# Revit family: VLN_Nim-II-Mes-E_Multiproduct_BIM_NL_F3054;F3055
name_source: partatom
category: Plumbing Fixtures
revit_build: Autodesk Revit MEP 2014 (Build: 20130308_1515(x64)
units: mm (PartAtom-declared; Revit-internal decimal feet)

## types (2) — shared parameters
Accessories = www.idealstandardnederland.nl
AreaUnits = millimeters
Assembly Code = C1030200
AssetType = Vast
BREEAMApproved = No
Brand = Venlo
CodePerformance = EN 817, DIN 4109
Color = Chroom
ConnectionType = Sanitair
Default Elevation = 800 mm  [stored 2.62467 ft]
DurationUnit = jaar
ECA = No
ExpectedLife = 25
FaucetFunction = Mengkraan
FaucetOperation = Tweegreeps
FaucetType = Keukenmengkraan
Finish = Chroom
IfcExportAs = IfcValveType
IfcExportType = FAUCET
InstallationInstructions = http://www.idealstandardnederland.nl
LinearUnits = millimeters
ManufacturerURL = www.idealstandardnederland.nl
Material = Messing
NBSDescription = Water supply fittings for sinks
NBSReference = 45-35-70/345
NettWeight = 1.263 kg
NominalHeight = 297 mm
NominalLength = 217 mm
NominalWidth = 143 mm
ProductInformation = http://www.idealstandardnederland.nl
Shape = Gesculptuurd
Size = 143 x 217 x 297 mm
Space = Internal
SpareParts = www.idealstandardnederland.nl
TMV3 = Yes
TestPressure = 10 Bar
URL = www.idealstandardnederland.nl
Uniclass2015Code = Pr_40_20_87_84
Uniclass2015Title = Sink taps
Uniclass2015Version = Products v1.1
ValveMechanism = Keramische schijven
ValveOperation = Tweegreeps
Version = 1
VolumeUnits = liter
WRAS = No
WarrantyDescription = Fabrieksgarantie
WarrantyDurationParts = 10
WarrantyDurationUnit = jaar
WaterEfficientProduct = No
WorkingPressure = 1-5 bar
zero-valued in all types: CWFU, Cost, HWFU, WFU

## per-type parameters (varying)
| type | BIMObjectName | BarCode | Description | Features | FlowRate | Model | ModelNumber | ModelReference | Name |
| F3054AA - NIM-II-MES-E OPM T.FIX KEUKEN M KR 5L/MI | VLN_Venlo_SinkTaps_F3054AA | 8711678064721 | Venlo Nimbus II Messing keukenmengkraan 5 l/min eco. Eengats. Hoge draaibare uitloop. Straalregelaar. Sprong 200 mm. Hoogte uitloop 185 mm. Bovenbevestiging (TOP FIX). Eco bovendelen. Verloopset separaat bestellen. | Keukenmengkraan 5 l/min eco. Eengats. Hoge draaibare uitloop. Straalregelaar. Sprong 200 mm. Hoogte uitloop 185 mm. Bovenbevestiging (TOP FIX). Eco bovendelen. Verloopset separaat bestellen. | 5 liter @ 3 bar | F3054AA | F3054AA | Venlo Nimbus II Messing keukenmengkraan 5 l/min eco. Eengats. Hoge draaibare uitloop. Straalregelaar. Sprong 200 mm. Hoogte uitloop 185 mm. Bovenbevestiging (TOP FIX). Eco bovendelen. Verloopset separaat bestellen. | SinkTaps_F3054AA_Venlo |
| F3055AA - NIM-II-MES-E OPM TOPFLEX KEUKEN M KR 1-G | VLN_Venlo_SinkTaps_F3055AA | 8711678062932 | Venlo Nimbus II Messing keukenmengkraan eco. Eengats. Hoge draaibare uitloop. Straalregelaar. Sprong 200 mm. Hoogte uitloop 185 mm. Bovenbevestiging (TOP FIX). Eco bovendelen. Verloopset separaat bestellen. | Keukenmengkraan eco. Eengats. Hoge draaibare uitloop. Straalregelaar. Sprong 200 mm. Hoogte uitloop 185 mm. Bovenbevestiging (TOP FIX). Eco bovendelen. Verloopset separaat bestellen. |  | F3055AA | F3055AA | Venlo Nimbus II Messing keukenmengkraan eco. Eengats. Hoge draaibare uitloop. Straalregelaar. Sprong 200 mm. Hoogte uitloop 185 mm. Bovenbevestiging (TOP FIX). Eco bovendelen. Verloopset separaat bestellen. | SinkTaps_F3055AA_Venlo |

note: [stored X ft] marks values corroborated as IEEE doubles in the binary element streams (Revit-internal decimal feet)

## geometry (parser evidence)
native form markers: Sweep x1
no freeform markers — native parametric forms only
